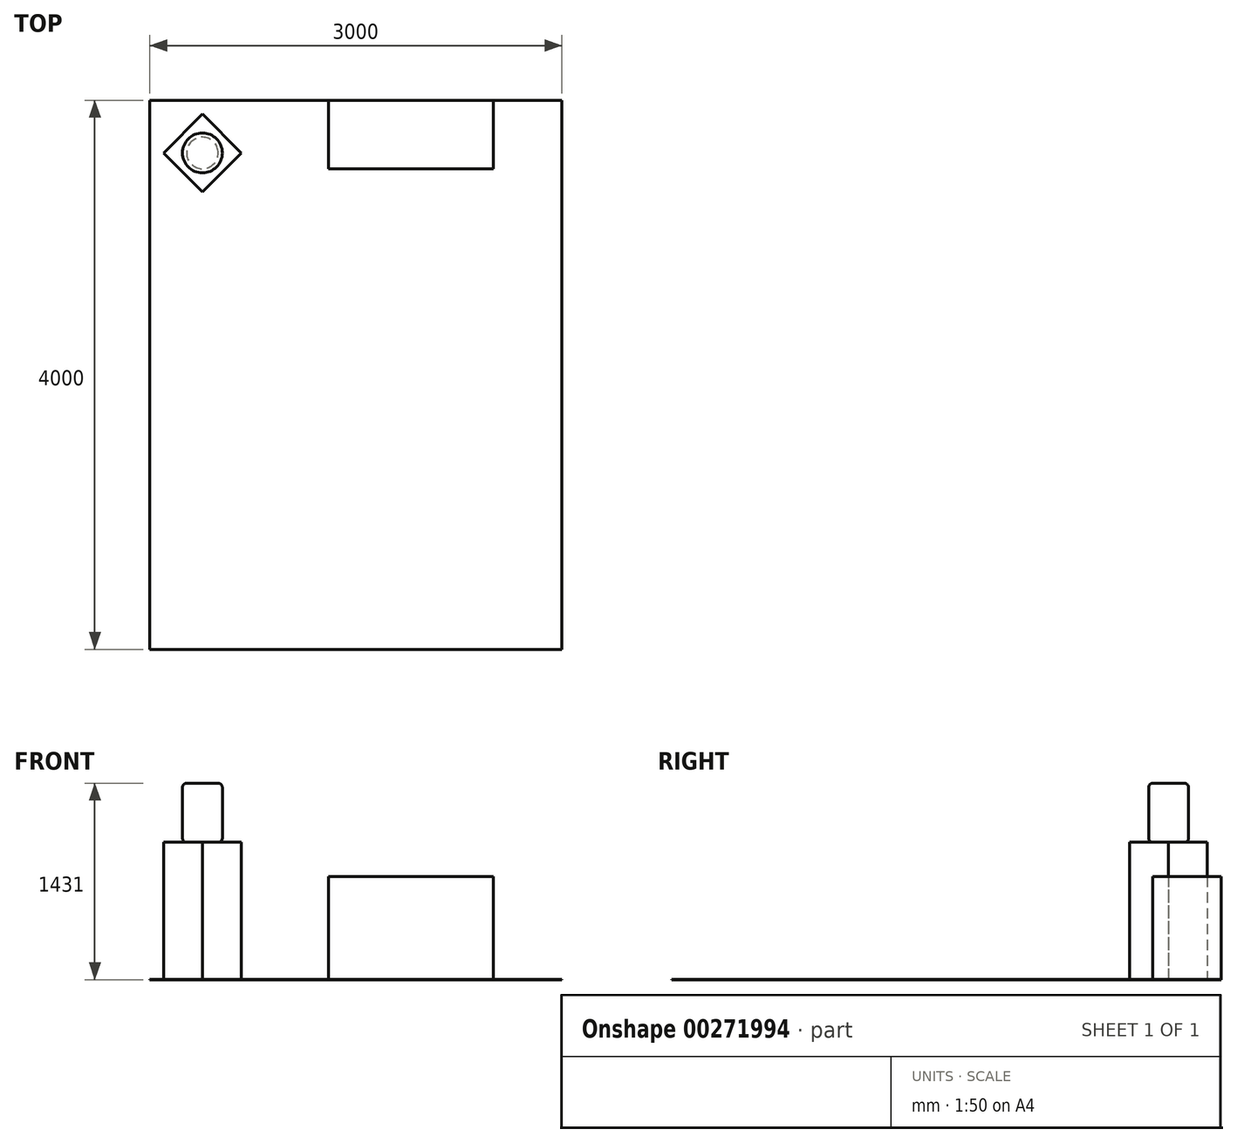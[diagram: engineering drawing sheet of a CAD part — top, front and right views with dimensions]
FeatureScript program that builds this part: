
annotation { "Feature Type Name" : "Feature", "Feature Type Description" : "" }
export const myFeature = defineFeature(function(context is Context, id is Id, definition is map)
    precondition{}
    {
        {
            var Q0;
            Q0=qCreatedBy(makeId("Top.planeOp"),FACE);
            var sketch = newSketch(context, id + "F0", { "sketchPlane" : qUnion([Q0])});
            skLineSegment(sketch, "E0.bottom", {"start": v(0, 0) * mm, "end": v(3000, 0) * mm});
            skLineSegment(sketch, "E0.top", {"start": v(0, 4000) * mm, "end": v(3000, 4000) * mm});
            skLineSegment(sketch, "E0.left", {"start": v(0, 0) * mm, "end": v(0, 4000) * mm});
            skLineSegment(sketch, "E0.right", {"start": v(3000, 0) * mm, "end": v(3000, 4000) * mm});
            skSolve(sketch);
        }
        {
            var Q0;
            Q0=sQuery(id+"F0.wireOp",EDGE,"E0.left");
            var Q1;
            Q1=sQuery(id+"F0.wireOp",EDGE,"E0.top");
            extrude(context, id + "F1", {"bodyType" : ToolBodyType.SURFACE, "surfaceEntities" : qUnion([Q0, Q1]), "depth" : 2000 * mm});
        }
        {
            var Q0;
            Q0=makeQuery(id+"F0.imprint","IMPRINT",FACE,{"disambiguationData":[TD([[makeQuery(id+"F0.imprint","IMPRINT",EDGE,{"derivedFrom":sQuery(id+"F0.wireOp",EDGE,"E0.bottom")}),1.0]])]});
            extrude(context, id + "F2", {"entities" : qUnion([Q0]), "oppositeDirection" : true, "depth" : 1 * mm});
        }
        {
            var Q0;
            Q0=makeQuery(id+"F2.opExtrude","CAP_FACE",FACE,{"disambiguationData":[OSD([sQuery(id+"F0.wireOp",EDGE,"E0.bottom"),sQuery(id+"F0.wireOp",EDGE,"E0.top"),sQuery(id+"F0.wireOp",EDGE,"E0.left"),sQuery(id+"F0.wireOp",EDGE,"E0.right")])],"isStart":true});
            var sketch = newSketch(context, id + "F3", { "sketchPlane" : qUnion([Q0])});
            skLineSegment(sketch, "E1.bottom", {"start": v(1300, 4000) * mm, "end": v(2500, 4000) * mm});
            skLineSegment(sketch, "E1.top", {"start": v(1300, 3500) * mm, "end": v(2500, 3500) * mm});
            skLineSegment(sketch, "E1.left", {"start": v(1300, 4000) * mm, "end": v(1300, 3500) * mm});
            skLineSegment(sketch, "E1.right", {"start": v(2500, 4000) * mm, "end": v(2500, 3500) * mm});
            skSolve(sketch);
        }
        {
            var Q0;
            Q0=qCreatedBy(makeId("Top.planeOp"),FACE);
            var sketch = newSketch(context, id + "F4", { "sketchPlane" : qUnion([Q0])});
            skLineSegment(sketch, "E2.bottom", {"start": v(382.84, 3900) * mm, "end": v(100, 3617.16) * mm});
            skLineSegment(sketch, "E2.top", {"start": v(665.69, 3617.16) * mm, "end": v(382.84, 3334.31) * mm});
            skLineSegment(sketch, "E2.left", {"start": v(382.84, 3900) * mm, "end": v(665.69, 3617.16) * mm});
            skLineSegment(sketch, "E2.right", {"start": v(100, 3617.16) * mm, "end": v(382.84, 3334.31) * mm});
            skSolve(sketch);
        }
        {
            var Q0;
            Q0 = qSketchRegion(id + "F4", true);
            extrude(context, id + "F5", {"entities" : qUnion([Q0]), "operationType" : NewBodyOperationType.ADD, "depth" : 1000 * mm});
        }
        {
            var Q0;
            Q0 = qSketchRegion(id + "F3", true);
            extrude(context, id + "F6", {"entities" : qUnion([Q0]), "operationType" : NewBodyOperationType.ADD, "depth" : 750 * mm});
        }
        {
            var Q0;
            Q0=makeQuery(id+"F5.opExtrude","SWEPT_FACE",FACE,{"disambiguationData":[OSD([sQuery(id+"F4.wireOp",EDGE,"E2.top")])]});
            cPlane(context, id + "F7", {"entities" : qUnion([Q0]), "cplaneType" : CPlaneType.OFFSET, "offset" : 200 * mm, "oppositeDirection" : true, "width" : 150 * mm, "height" : 150 * mm});
        }
        {
            var Q0;
            Q0=qCreatedBy(id+"F7.planeOp",FACE);
            var sketch = newSketch(context, id + "F8", { "sketchPlane" : qUnion([Q0])});
            skLineSegment(sketch, "E3", {"start": v(2828.43, 900) * mm, "end": v(2828.43, 1430) * mm});
            skLineSegment(sketch, "E4", {"start": v(2828.43, 1430) * mm, "end": v(2713.43, 1430) * mm});
            skLineSegment(sketch, "E5", {"start": v(2683.43, 1400) * mm, "end": v(2683.43, 1030) * mm});
            skLineSegment(sketch, "E6", {"start": v(2713.43, 1000) * mm, "end": v(2803.43, 1000) * mm});
            skLineSegment(sketch, "E7", {"start": v(2803.43, 1000) * mm, "end": v(2803.43, 900) * mm});
            skLineSegment(sketch, "E8", {"start": v(2803.43, 900) * mm, "end": v(2828.43, 900) * mm});
            skPoint(sketch, "E9.visualSharp", {"position": v(2683.43, 1430) * mm});
            skArc(sketch, "E9.filletArc", {"start": v(2713.43, 1430) * mm, "mid": v(2692.21, 1421.21) * mm, "end": v(2683.43, 1400) * mm});
            skPoint(sketch, "E10.visualSharp", {"position": v(2683.43, 1000) * mm});
            skArc(sketch, "E10.filletArc", {"start": v(2683.43, 1030) * mm, "mid": v(2692.21, 1008.79) * mm, "end": v(2713.43, 1000) * mm});
            skSolve(sketch);
        }
        {
            var Q0;
            Q0=makeQuery(id+"F8.imprint","IMPRINT",FACE,{"disambiguationData":[TD([[makeQuery(id+"F8.imprint","IMPRINT",EDGE,{"derivedFrom":sQuery(id+"F8.wireOp",EDGE,"E3")}),1.0]])]});
            var Q1;
            Q1=sQuery(id+"F8.wireOp",EDGE,"E3");
            revolve(context, id + "F9", {"operationType" : NewBodyOperationType.ADD, "entities" : qUnion([Q0]), "axis" : qUnion([Q1]), "revolveType" : RevolveType.FULL});
        }
    });
